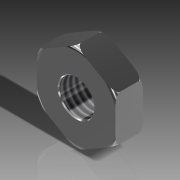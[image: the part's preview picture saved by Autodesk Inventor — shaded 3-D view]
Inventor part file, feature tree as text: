
AUTODESK INVENTOR PART (.ipt)
format: ipt  version: 2011 (Build 150239000, 239)  size: 148,480 bytes
history: native  units: in
note: dims shown in document units (in); Inventor stores cm internally (conversion verified against a paired STEP export)
features: other x1, imported_body x1, thread x1
ambient origin geometry x8: Origin, YZ Plane, XZ Plane, XY Plane, X Axis, Y Axis, Z Axis, Center Point
feature tree (3):
  parser-record x1  (decoder bookkeeping rows leaked as tree rows — omitted from the tree; the rows remain in map.json)
  imported_body  "Base1"
  thread  "Thread1"  [1 undecoded]
note: 1 required parameter value undecoded (feature->parameter linkage not recoverable at this tier; creation-order binding heuristic only, values carry confidence <= 0.55)
